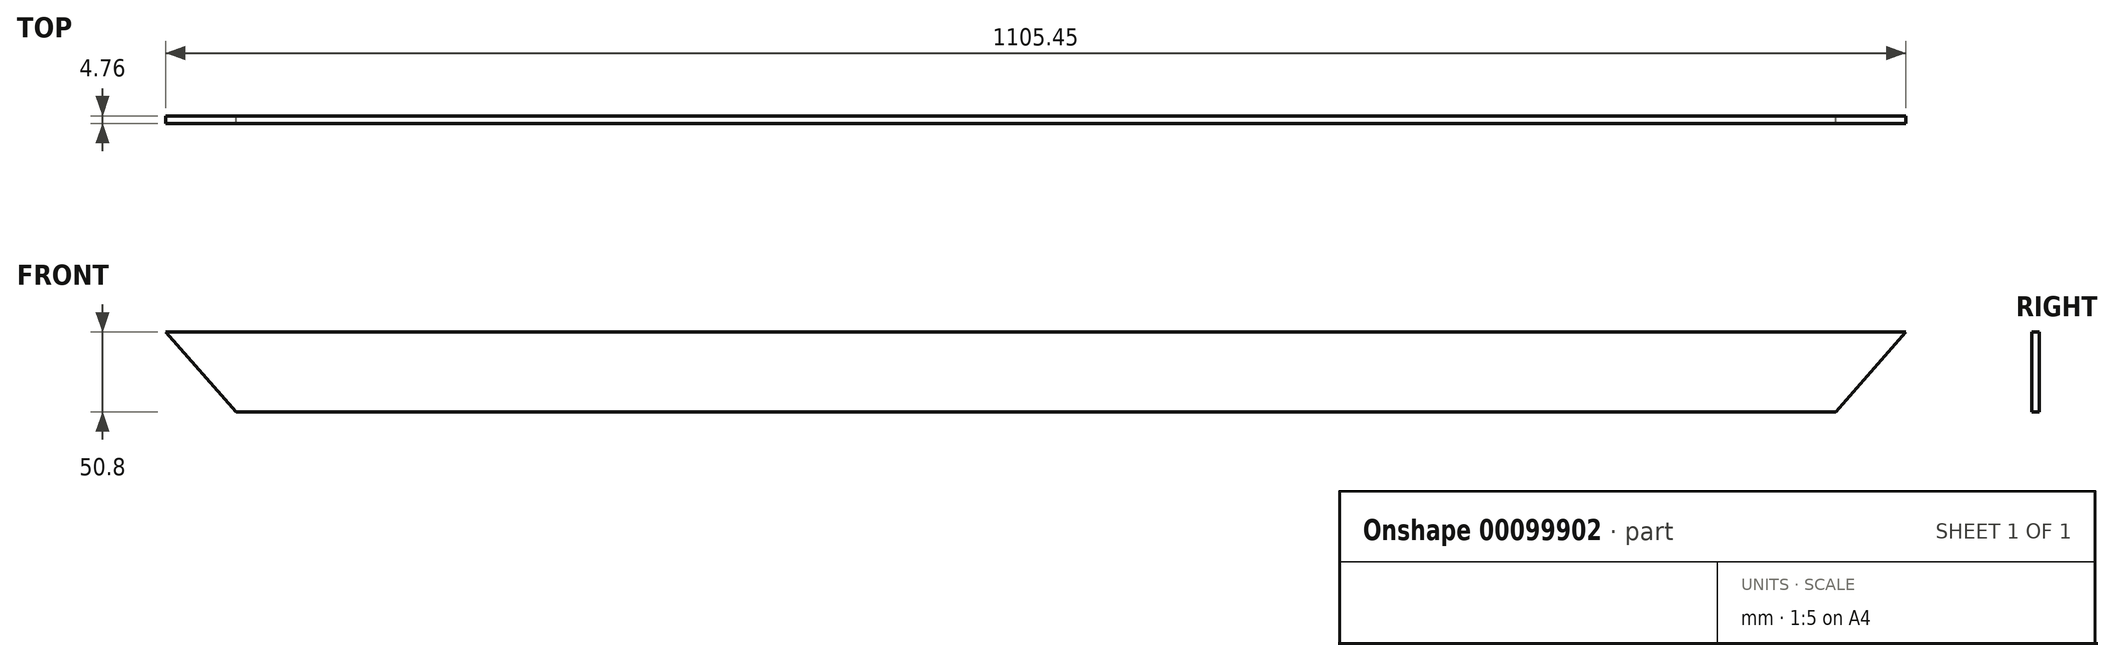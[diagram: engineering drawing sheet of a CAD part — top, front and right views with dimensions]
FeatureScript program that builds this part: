
annotation { "Feature Type Name" : "Feature", "Feature Type Description" : "" }
export const myFeature = defineFeature(function(context is Context, id is Id, definition is map)
    precondition{}
    {
        {
            var Q0;
            Q0=qCreatedBy(makeId("Front.planeOp"),FACE);
            var sketch = newSketch(context, id + "F0", { "sketchPlane" : qUnion([Q0])});
            skLineSegment(sketch, "E0", {"start": v(-138.69, 0) * mm, "end": v(877.31, 0) * mm});
            skLineSegment(sketch, "E1", {"start": v(877.31, 0) * mm, "end": v(922.04, 50.8) * mm});
            skLineSegment(sketch, "E2", {"start": v(922.04, 50.8) * mm, "end": v(-183.4, 50.8) * mm});
            skLineSegment(sketch, "E3", {"start": v(-183.4, 50.8) * mm, "end": v(-138.69, 0) * mm});
            skSolve(sketch);
        }
        {
            var Q0;
            Q0 = qSketchRegion(id + "F0", true);
            extrude(context, id + "F1", {"entities" : qUnion([Q0]), "depth" : 4.76 * mm});
        }
    });
